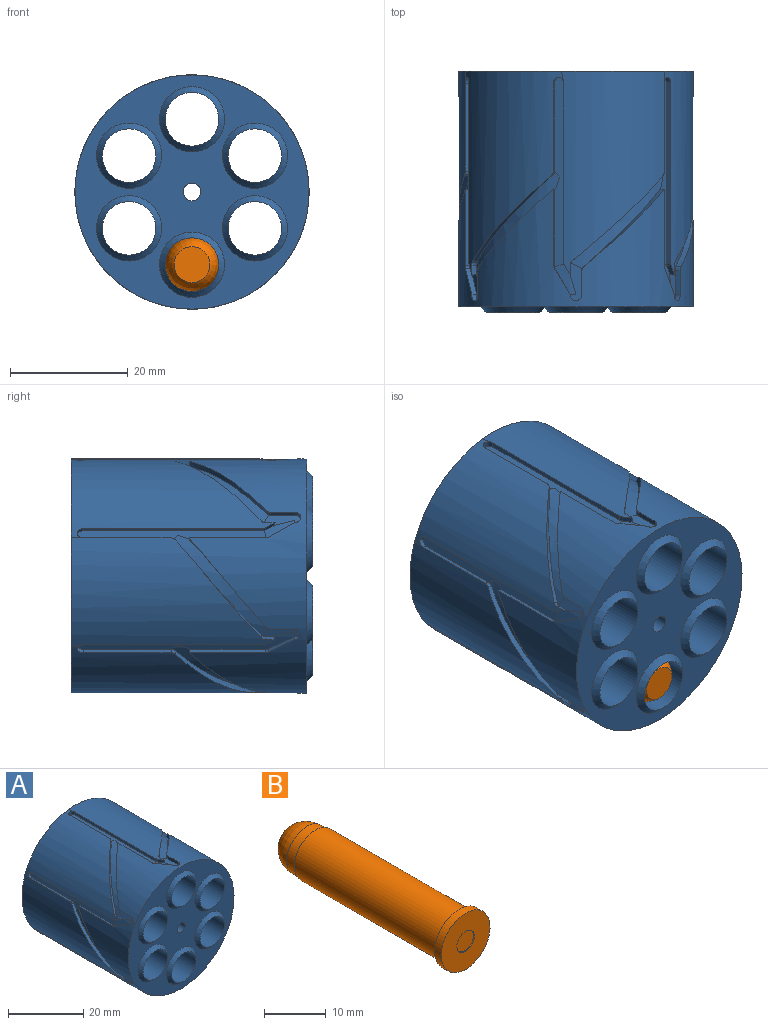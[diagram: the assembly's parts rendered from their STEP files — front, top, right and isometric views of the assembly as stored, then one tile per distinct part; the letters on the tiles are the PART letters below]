
ASSEMBLY  parts=2 mates=1
PART A: 173 faces, bbox 42.5x41x42.7 mm
  f0: cylinder r=1.5mm len=39mm, axis (0,-1,0), area 367.6mm2, adj f17,f171
  f1: cylinder r=4.9mm len=33mm, axis (0,-1,0), area 1016mm2, adj f149,f164
  f2: cylinder r=4.9mm len=33mm, axis (0,-1,0), area 1016mm2, adj f147,f162
  f3: cylinder r=4.9mm len=33mm, axis (0,-1,0), area 1016mm2, adj f145,f160
  f4: cylinder r=4.9mm len=33mm, axis (0,-1,0), area 1016mm2, adj f143,f158
  f5: cylinder r=4.9mm len=33mm, axis (0,-1,0), area 1016mm2, adj f141,f156
  f6: cylinder r=4.9mm len=33mm, axis (0,-1,0), area 1016mm2, adj f151,f154
  f7: plane 30.49x0.97mm, normal (-0.99,0,-0.15), area 29.9mm2, adj f13,f15,f110,f137
  f8: plane 30.49x0.91mm, normal (-0.37,0,-0.93), area 29.9mm2, adj f15,f87,f108,f113
  f9: plane 30.49x0.77mm, normal (-0.62,0,0.78), area 29.9mm2, adj f15,f35,f106,f132
  f10: plane 30.49x0.91mm, normal (0.37,0,0.93), area 29.9mm2, adj f15,f48,f104,f127
  f11: plane 30.49x0.97mm, normal (0.99,0,0.15), area 29.9mm2, adj f15,f61,f102,f124
  f12: plane 30.49x0.77mm, normal (0.62,0,-0.78), area 29.9mm2, adj f15,f74,f100,f119
  f13: plane 32.24x2.05mm, normal (-0.15,0,0.99), area 53.1mm2, adj f7,f14,f24,f26,f28,f83,f84,f85
  f14: plane 12.96x0.97mm, normal (0.99,0,0.15), area 12.7mm2, adj f13,f16,f84,f138
  f15: cylinder r=19.9mm len=39.8mm, axis (0,1,0), area 2939mm2, adj f7,f8,f9,f10,f11,f12,f19,f21
  f16: cylinder r=19.9mm len=39.8mm, axis (0,1,0), area 1360.8mm2, adj f14,f17,f18,f20,f25,f29,f31,f36
  f17: plane 39.8x39.8mm, normal (0,-1,0), area 656.4mm2, adj f0,f16,f165,f166,f167,f168,f169,f170
  f18: bspline ~19.69x18.91mm, area 19.8mm2, adj f16,f22,f23,f35,f37,f140
  f19: bspline ~17.05x15.39mm, area 22.1mm2, adj f15,f22,f35,f131,f139
  f20: plane 4.09x0.98mm, normal (-1,0,0), area 4mm2, adj f16,f23,f136,f140
  f21: plane 1.65x0.98mm, normal (1,0,0), area 1.5mm2, adj f15,f23,f27,f28,f139
  f22: bspline ~16.96x16.31mm, area 44.4mm2, adj f18,f19,f23,f35,f139
  f23: plane 6.47x2.39mm, normal (0,0,1), area 9.8mm2, adj f18,f20,f21,f22,f28,f136,f139,f140
  f24: plane 0.28x0mm, normal (-0.99,0,-0.15), area 0mm2, adj f13,f28
  f25: bspline ~10.5x6.41mm, area 5.1mm2, adj f16,f28,f136,f138
  f26: plane 14.97x0.97mm, normal (0.99,0,0.15), area 14.7mm2, adj f13,f15,f111,f115
  f27: bspline ~3.68x2.39mm, area 1.8mm2, adj f15,f21,f28,f137
  f28: bspline ~5.54x5.32mm, area 8.2mm2, adj f13,f21,f23,f24,f25,f27,f137,f138
  f29: bspline ~23.13x19.69mm, area 19.8mm2, adj f16,f33,f34,f48,f51,f135
  f30: bspline ~18.45x15.39mm, area 22mm2, adj f15,f33,f48,f126,f134
  f31: plane 4.09x0.84mm, normal (-0.5,0,0.87), area 4mm2, adj f16,f34,f99,f135
  f32: plane 1.65x0.85mm, normal (0.5,0,-0.87), area 1.5mm2, adj f15,f34,f40,f41,f134
  f33: bspline ~17.94x16.96mm, area 44.4mm2, adj f29,f30,f34,f48,f134
  f34: plane 6.47x2.07mm, normal (0.87,0,0.5), area 9.8mm2, adj f29,f31,f32,f33,f41,f99,f134,f135
  f35: plane 32.23x1.62mm, normal (0.78,0,0.62), area 53.1mm2, adj f9,f18,f19,f22,f37,f38,f39,f41
  f36: bspline ~4.53x2.65mm, area 5.1mm2, adj f16,f41,f99,f133
  f37: plane 12.96x0.77mm, normal (0.62,0,-0.78), area 12.7mm2, adj f16,f18,f35,f133
  f38: plane 14.97x0.77mm, normal (0.62,0,-0.78), area 14.7mm2, adj f15,f35,f107,f131
  f39: plane 0.28x0mm, normal (-0.62,0,0.78), area 0mm2, adj f35,f41
  f40: bspline ~3.68x2.99mm, area 1.8mm2, adj f15,f32,f41,f132
  f41: bspline ~5.51x4.37mm, area 8.2mm2, adj f32,f34,f35,f36,f39,f40,f132,f133
  f42: bspline ~21.14x19.69mm, area 19.8mm2, adj f16,f46,f47,f61,f64,f130
  f43: bspline ~15.39x15.2mm, area 22mm2, adj f15,f46,f61,f123,f129
  f44: plane 4.09x0.84mm, normal (0.5,0,0.87), area 4mm2, adj f16,f47,f98,f130
  f45: plane 1.65x0.85mm, normal (-0.5,0,-0.87), area 1.5mm2, adj f15,f47,f53,f54,f129
  f46: bspline ~16.96x14.76mm, area 44.4mm2, adj f42,f43,f47,f61,f129
  f47: plane 6.47x2.07mm, normal (0.87,0,-0.5), area 9.8mm2, adj f42,f44,f45,f46,f54,f98,f129,f130
  f48: plane 32.23x1.92mm, normal (0.93,0,-0.37), area 53.1mm2, adj f10,f29,f30,f33,f50,f51,f52,f54
  f49: bspline ~10.5x6.63mm, area 5.1mm2, adj f16,f54,f98,f128
  f50: plane 0.28x0mm, normal (0.37,0,0.93), area 0mm2, adj f48,f54
  f51: plane 12.96x0.92mm, normal (-0.37,0,-0.93), area 12.7mm2, adj f16,f29,f48,f128
  f52: plane 14.97x0.91mm, normal (-0.37,0,-0.93), area 14.7mm2, adj f15,f48,f105,f126
  f53: bspline ~3.68x2.8mm, area 1.8mm2, adj f15,f45,f54,f127
  f54: bspline ~5.54x4.82mm, area 8.2mm2, adj f45,f47,f48,f49,f50,f53,f127,f128
  f55: bspline ~19.69x18.91mm, area 20.3mm2, adj f16,f57,f59,f74,f77
  f56: bspline ~17.05x15.39mm, area 22.3mm2, adj f15,f58,f59,f74,f118
  f57: plane 4.56x0.99mm, normal (1,0,0), area 4.4mm2, adj f16,f55,f60,f97
  f58: plane 2.11x0.98mm, normal (-1,0,0), area 2mm2, adj f15,f56,f60,f66,f67
  f59: bspline ~16.96x16.31mm, area 44.4mm2, adj f55,f56,f60,f74
  f60: plane 6.51x2.05mm, normal (0,0,-1), area 9.8mm2, adj f57,f58,f59,f67,f97
  f61: plane 32.23x2.04mm, normal (0.15,0,-0.99), area 53.1mm2, adj f11,f42,f43,f46,f63,f64,f65,f67
  f62: bspline ~10.5x6.41mm, area 5.1mm2, adj f16,f67,f97,f125
  f63: plane 0.28x0mm, normal (0.99,0,0.15), area 0mm2, adj f61,f67
  f64: plane 12.96x0.97mm, normal (-0.99,0,-0.15), area 12.7mm2, adj f16,f42,f61,f125
  f65: plane 14.97x0.97mm, normal (-0.99,0,-0.15), area 14.7mm2, adj f15,f61,f103,f123
  f66: bspline ~3.68x2.39mm, area 1.8mm2, adj f15,f58,f67,f124
  f67: bspline ~5.54x5.32mm, area 8.2mm2, adj f58,f60,f61,f62,f63,f66,f124,f125
  f68: bspline ~23.13x19.69mm, area 19.8mm2, adj f16,f72,f73,f87,f90,f122
  f69: bspline ~18.45x15.39mm, area 22mm2, adj f15,f72,f87,f112,f121
  f70: plane 4.09x0.84mm, normal (0.5,0,-0.87), area 4mm2, adj f16,f73,f96,f122
  f71: plane 1.65x0.85mm, normal (-0.5,0,0.87), area 1.5mm2, adj f15,f73,f79,f80,f121
  f72: bspline ~17.94x16.96mm, area 44.4mm2, adj f68,f69,f73,f87,f121
  f73: plane 6.47x2.07mm, normal (-0.87,0,-0.5), area 9.8mm2, adj f68,f70,f71,f72,f80,f96,f121,f122
  f74: plane 32.23x1.62mm, normal (-0.78,0,-0.62), area 53.1mm2, adj f12,f55,f56,f59,f76,f77,f78,f80
  f75: bspline ~4.53x2.65mm, area 5.1mm2, adj f16,f80,f96,f120
  f76: plane 0.28x0mm, normal (0.62,0,-0.78), area 0mm2, adj f74,f80
  f77: plane 12.96x0.77mm, normal (-0.62,0,0.78), area 12.7mm2, adj f16,f55,f74,f120
  f78: plane 14.97x0.77mm, normal (-0.62,0,0.78), area 14.7mm2, adj f15,f74,f101,f118
  f79: bspline ~3.68x2.99mm, area 1.8mm2, adj f15,f71,f80,f119
  f80: bspline ~5.51x4.37mm, area 8.2mm2, adj f71,f73,f74,f75,f76,f79,f119,f120
  f81: plane 4.09x0.84mm, normal (-0.5,0,-0.87), area 4mm2, adj f16,f86,f95,f117
  f82: plane 1.65x0.85mm, normal (0.5,0,0.87), area 1.5mm2, adj f15,f86,f92,f93,f116
  f83: bspline ~16.96x14.76mm, area 44.4mm2, adj f13,f84,f85,f86,f116
  f84: bspline ~21.14x19.69mm, area 19.8mm2, adj f13,f14,f16,f83,f86,f117
  f85: bspline ~15.39x15.2mm, area 22mm2, adj f13,f15,f83,f115,f116
  f86: plane 6.47x2.07mm, normal (-0.87,0,0.5), area 9.8mm2, adj f81,f82,f83,f84,f93,f95,f116,f117
  f87: plane 32.23x1.92mm, normal (-0.93,0,0.37), area 53.1mm2, adj f8,f68,f69,f72,f89,f90,f91,f93
  f88: bspline ~10.5x6.63mm, area 5.1mm2, adj f16,f93,f95,f114
  f89: plane 0.28x0mm, normal (-0.37,0,-0.93), area 0mm2, adj f87,f93
  f90: plane 12.96x0.92mm, normal (0.37,0,0.93), area 12.7mm2, adj f16,f68,f87,f114
  f91: plane 14.97x0.91mm, normal (0.37,0,0.93), area 14.7mm2, adj f15,f87,f109,f112
  f92: bspline ~3.68x2.8mm, area 1.8mm2, adj f15,f82,f93,f113
  f93: bspline ~5.54x4.82mm, area 8.2mm2, adj f82,f86,f87,f88,f89,f92,f113,f114
  f94: plane 39.8x39.8mm, normal (0,1,0), area 640.4mm2, adj f15,f142,f144,f146,f148,f150,f152,f172
  f95: cylinder r=1mm len=2.23mm, axis (-0.87,0,0.5), area 3.1mm2, adj f16,f81,f86,f88
  f96: cylinder r=1mm len=2.23mm, axis (-0.87,0,-0.5), area 3.1mm2, adj f16,f70,f73,f75
  f97: cylinder r=1mm len=2mm, axis (0,0,-1), area 3.1mm2, adj f16,f57,f60,f62
  f98: cylinder r=1mm len=2.23mm, axis (-0.87,0,0.5), area 3.1mm2, adj f16,f44,f47,f49
  f99: cylinder r=1mm len=2.23mm, axis (0.87,0,0.5), area 3.1mm2, adj f16,f31,f34,f36
  f100: cylinder r=1mm len=1.32mm, axis (0.78,0,0.62), area 1.4mm2, adj f12,f15,f74,f101
  f101: cylinder r=1mm len=1.32mm, axis (-0.78,0,-0.62), area 1.4mm2, adj f15,f74,f78,f100
  f102: cylinder r=1mm len=1.12mm, axis (-0.15,0,0.99), area 1.4mm2, adj f11,f15,f61,f103
  f103: cylinder r=1mm len=1.12mm, axis (0.15,0,-0.99), area 1.4mm2, adj f15,f61,f65,f102
  f104: cylinder r=1mm len=1.24mm, axis (-0.93,0,0.37), area 1.4mm2, adj f10,f15,f48,f105
  f105: cylinder r=1mm len=1.24mm, axis (0.93,0,-0.37), area 1.4mm2, adj f15,f48,f52,f104
  f106: cylinder r=1mm len=1.32mm, axis (-0.78,0,-0.62), area 1.4mm2, adj f9,f15,f35,f107
  f107: cylinder r=1mm len=1.32mm, axis (0.78,0,0.62), area 1.4mm2, adj f15,f35,f38,f106
  f108: cylinder r=1mm len=1.24mm, axis (0.93,0,-0.37), area 1.4mm2, adj f8,f15,f87,f109
  f109: cylinder r=1mm len=1.24mm, axis (-0.93,0,0.37), area 1.4mm2, adj f15,f87,f91,f108
  f110: cylinder r=1mm len=1.12mm, axis (-0.15,0,0.99), area 1.4mm2, adj f7,f13,f15,f111
  f111: cylinder r=1mm len=1.12mm, axis (-0.15,0,0.99), area 1.4mm2, adj f13,f15,f26,f110
  f112: bspline ~1.31x0.78mm, area 0.8mm2, adj f15,f69,f87,f91
  f113: bspline ~1.26x0.61mm, area 0.5mm2, adj f8,f15,f92,f93
  f114: bspline ~1.19x0.59mm, area 0.5mm2, adj f16,f87,f88,f90,f93
  f115: bspline ~1.27x0.78mm, area 0.8mm2, adj f13,f15,f26,f85
  f116: bspline ~1.37x1mm, area 0.9mm2, adj f15,f82,f83,f85,f86
  f117: bspline ~1.24x0.95mm, area 0.8mm2, adj f16,f81,f84,f86
  f118: bspline ~1.18x1.07mm, area 0.8mm2, adj f15,f56,f74,f78
  f119: bspline ~1.24x1.03mm, area 0.5mm2, adj f12,f15,f79,f80
  f120: bspline ~1.07x0.87mm, area 0.5mm2, adj f16,f74,f75,f77,f80
  f121: bspline ~1.37x0.99mm, area 0.9mm2, adj f15,f69,f71,f72,f73
  f122: bspline ~1.28x0.91mm, area 0.8mm2, adj f16,f68,f70,f73
  f123: bspline ~1.28x0.78mm, area 0.8mm2, adj f15,f43,f61,f65
  f124: bspline ~1.31x0.51mm, area 0.5mm2, adj f11,f15,f66,f67
  f125: bspline ~1.26x0.52mm, area 0.5mm2, adj f16,f61,f62,f64,f67
  f126: bspline ~1.31x0.78mm, area 0.8mm2, adj f15,f30,f48,f52
  f127: bspline ~1.26x0.61mm, area 0.5mm2, adj f10,f15,f53,f54
  f128: bspline ~1.19x0.59mm, area 0.5mm2, adj f16,f48,f49,f51,f54
  f129: bspline ~1.37x1mm, area 0.9mm2, adj f15,f43,f45,f46,f47
  f130: bspline ~1.24x0.95mm, area 0.8mm2, adj f16,f42,f44,f47
  f131: bspline ~1.18x1.07mm, area 0.8mm2, adj f15,f19,f35,f38
  f132: bspline ~1.24x1.03mm, area 0.5mm2, adj f9,f15,f40,f41
  f133: bspline ~1.07x0.87mm, area 0.5mm2, adj f16,f35,f36,f37,f41
  f134: bspline ~1.37x0.99mm, area 0.9mm2, adj f15,f30,f32,f33,f34
  f135: bspline ~1.28x0.91mm, area 0.8mm2, adj f16,f29,f31,f34
  f136: cylinder r=1mm len=2mm, axis (0,0,-1), area 3.1mm2, adj f16,f20,f23,f25
  f137: bspline ~1.31x0.51mm, area 0.5mm2, adj f7,f15,f27,f28
  f138: bspline ~1.26x0.52mm, area 0.5mm2, adj f13,f14,f16,f25,f28
  f139: bspline ~1.38x0.77mm, area 0.9mm2, adj f15,f19,f21,f22,f23
  f140: bspline ~1.27x0.79mm, area 0.8mm2, adj f16,f18,f20,f23
  f141: plane 11.2x11.2mm, normal (0,1,0), area 23.1mm2, adj f5,f142
  f142: cylinder r=5.6mm len=11.2mm, axis (0,1,0), area 52.8mm2, adj f94,f141
  f143: plane 11.2x11.2mm, normal (0,1,0), area 23.1mm2, adj f4,f144
  f144: cylinder r=5.6mm len=11.2mm, axis (0,1,0), area 52.8mm2, adj f94,f143
  f145: plane 11.2x11.2mm, normal (0,1,0), area 23.1mm2, adj f3,f146
  f146: cylinder r=5.6mm len=11.2mm, axis (0,1,0), area 52.8mm2, adj f94,f145
  f147: plane 11.2x11.2mm, normal (0,1,0), area 23.1mm2, adj f2,f148
  f148: cylinder r=5.6mm len=11.2mm, axis (0,1,0), area 52.8mm2, adj f94,f147
  f149: plane 11.2x11.2mm, normal (0,1,0), area 23.1mm2, adj f1,f150
  f150: cylinder r=5.6mm len=11.2mm, axis (0,1,0), area 52.8mm2, adj f94,f149
  f151: plane 11.2x11.2mm, normal (0,1,0), area 23.1mm2, adj f6,f152
  f152: cylinder r=5.6mm len=11.2mm, axis (0,1,0), area 52.8mm2, adj f94,f151
  f153: cylinder r=4.55mm len=9.1mm, axis (0,-1,0), area 185.8mm2, adj f154,f170
  f154: plane 9.8x9.8mm, normal (0,1,0), area 10.4mm2, adj f6,f153
  f155: cylinder r=4.55mm len=9.1mm, axis (0,-1,0), area 185.8mm2, adj f156,f169
  f156: plane 9.8x9.8mm, normal (0,1,0), area 10.4mm2, adj f5,f155
  f157: cylinder r=4.55mm len=9.1mm, axis (0,-1,0), area 185.8mm2, adj f158,f168
  f158: plane 9.8x9.8mm, normal (0,1,0), area 10.4mm2, adj f4,f157
  f159: cylinder r=4.55mm len=9.1mm, axis (0,-1,0), area 185.8mm2, adj f160,f166
  f160: plane 9.8x9.8mm, normal (0,1,0), area 10.4mm2, adj f3,f159
  f161: cylinder r=4.55mm len=9.1mm, axis (0,-1,0), area 185.8mm2, adj f162,f165
  f162: plane 9.8x9.8mm, normal (0,1,0), area 10.4mm2, adj f2,f161
  f163: cylinder r=4.55mm len=9.1mm, axis (0,-1,0), area 185.8mm2, adj f164,f167
  f164: plane 9.8x9.8mm, normal (0,1,0), area 10.4mm2, adj f1,f163
  f165: cone r=4.55mm half-angle=45deg, axis (0,1,0), area 44.9mm2, adj f17,f161
  f166: cone r=4.55mm half-angle=45deg, axis (0,1,0), area 44.9mm2, adj f17,f159
  f167: cone r=4.55mm half-angle=45deg, axis (0,1,0), area 44.9mm2, adj f17,f163
  f168: cone r=4.55mm half-angle=45deg, axis (0,1,0), area 44.9mm2, adj f17,f157
  f169: cone r=4.55mm half-angle=45deg, axis (0,1,0), area 44.9mm2, adj f17,f155
  f170: cone r=4.55mm half-angle=45deg, axis (0,1,0), area 44.9mm2, adj f17,f153
  f171: plane 4x4mm, normal (0,1,0), area 5.5mm2, adj f0,f172
  f172: cylinder r=2mm len=4mm, axis (0,1,0), area 12.6mm2, adj f94,f171
PART B: 10 faces, bbox 11.2x40x11.2 mm
  f0: plane 6.1x6.1mm, normal (0,1,0), area 29.2mm2, adj f1
  f1: revolved ~9.1x9.1mm, area 99.3mm2, adj f0,f2
  f2: cylinder r=4.55mm len=9.1mm, axis (0,1,0), area 57.2mm2, adj f1,f3
  f3: plane 9.6x9.6mm, normal (0,1,0), area 7.3mm2, adj f2,f4
  f4: cylinder r=4.8mm len=33mm, axis (0,1,0), area 995.3mm2, adj f3,f5
  f5: plane 11.2x11.2mm, normal (0,1,0), area 26.1mm2, adj f4,f6
  f6: cylinder r=5.6mm len=11.2mm, axis (0,1,0), area 52.8mm2, adj f5,f7
  f7: plane 11.2x11.2mm, normal (0,-1,0), area 86mm2, adj f6,f8
  f8: cylinder r=2mm len=4mm, axis (0,-1,0), area 2.5mm2, adj f7,f9
  f9: plane 4x4mm, normal (0,-1,0), area 12.6mm2, adj f8
PLACE A t=(9.93,42.44,26.26)mm fixed
PLACE B rot(axis=(0,0,1),180deg) t=(9.93,60.44,13.91)mm
MATE slider B.f2 <-> A.f2  axis (0,-1,0) through (9.93,25.94,13.91)mm
